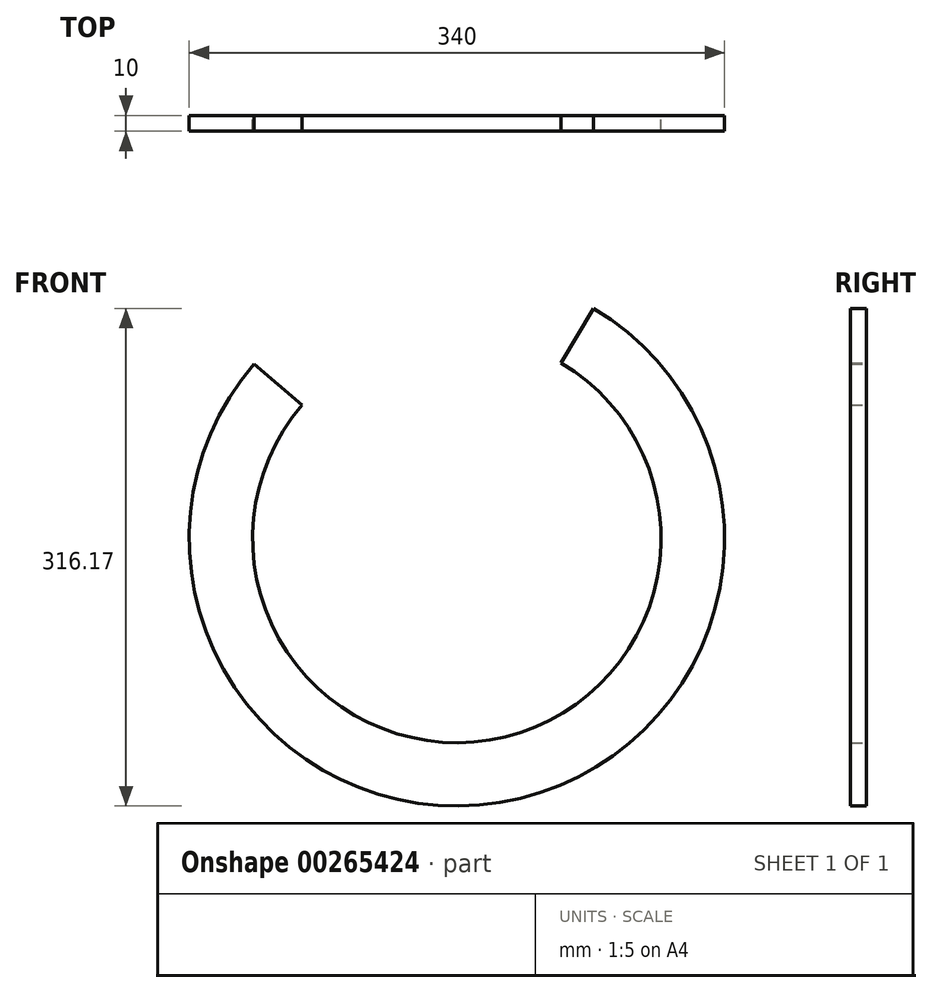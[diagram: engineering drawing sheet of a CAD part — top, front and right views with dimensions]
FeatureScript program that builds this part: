
annotation { "Feature Type Name" : "Feature", "Feature Type Description" : "" }
export const myFeature = defineFeature(function(context is Context, id is Id, definition is map)
    precondition{}
    {
        {
            var Q0;
            Q0=qCreatedBy(makeId("Front.planeOp"),FACE);
            var sketch = newSketch(context, id + "F0", { "sketchPlane" : qUnion([Q0])});
            skArc(sketch, "E0", {"start": v(-128.87, 110.87) * mm, "mid": v(27.46, -167.77) * mm, "end": v(86.8, 146.17) * mm});
            skArc(sketch, "E1", {"start": v(-98.36, 84.62) * mm, "mid": v(44.6, -121.85) * mm, "end": v(20.5, 128.12) * mm});
            skLineSegment(sketch, "E2", {"start": v(20.5, 128.12) * mm, "end": v(86.8, 146.17) * mm});
            skLineSegment(sketch, "E3", {"start": v(-98.36, 84.62) * mm, "end": v(-128.87, 110.87) * mm});
            skLineSegment(sketch, "E4", {"start": v(20.5, 128.12) * mm, "end": v(-98.36, 84.62) * mm});
            skLineSegment(sketch, "E5", {"start": v(-38.93, 106.37) * mm, "end": v(0, 0) * mm});
            skPoint(sketch, "E6.start.orphan", {"position": v(0, -129.75) * mm});
            skLineSegment(sketch, "E7", {"start": v(86.8, 146.17) * mm, "end": v(0, 0) * mm});
            skLineSegment(sketch, "E8", {"start": v(-128.87, 110.87) * mm, "end": v(0, 0) * mm});
            skSolve(sketch);
        }
        {
            var Q0;
            Q0=makeQuery(id+"F0.imprint","IMPRINT",FACE,{"disambiguationData":[TD([[makeQuery(id+"F0.imprint","IMPRINT",EDGE,{"derivedFrom":sQuery(id+"F0.wireOp",EDGE,"E0")}),1.0]])]});
            extrude(context, id + "F1", {"entities" : qUnion([Q0]), "depth" : 10 * mm});
        }
    });
